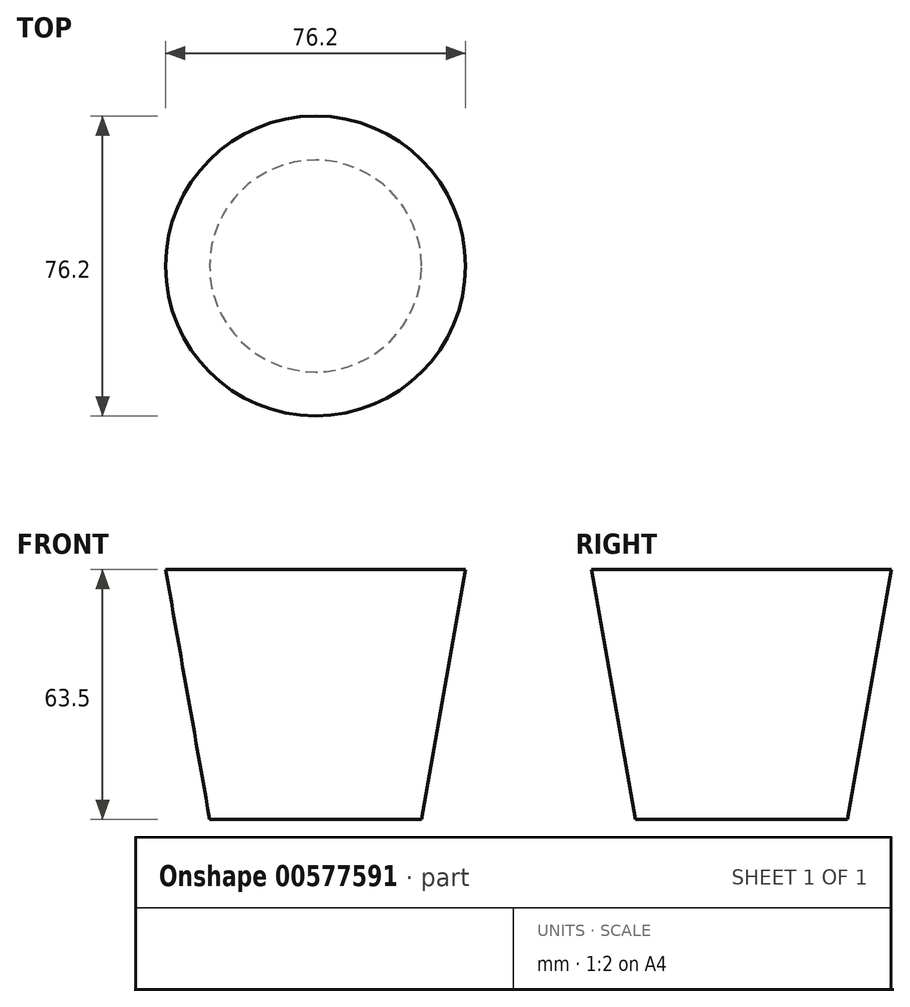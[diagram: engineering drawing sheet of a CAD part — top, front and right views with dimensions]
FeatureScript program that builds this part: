
annotation { "Feature Type Name" : "Feature", "Feature Type Description" : "" }
export const myFeature = defineFeature(function(context is Context, id is Id, definition is map)
    precondition{}
    {
        {
            var Q0;
            Q0=qCreatedBy(makeId("Front.planeOp"),FACE);
            var sketch = newSketch(context, id + "F0", { "sketchPlane" : qUnion([Q0])});
            skLineSegment(sketch, "E0", {"start": v(0, 63.5) * mm, "end": v(-38.1, 63.5) * mm});
            skLineSegment(sketch, "E1", {"start": v(-38.1, 63.5) * mm, "end": v(-26.9, 0) * mm});
            skLineSegment(sketch, "E2", {"start": v(-26.9, 0) * mm, "end": v(0, 0) * mm});
            skLineSegment(sketch, "E3", {"start": v(0, 0) * mm, "end": v(0, 63.5) * mm});
            skSolve(sketch);
        }
        {
            var Q0;
            Q0=makeQuery(id+"F0.imprint","IMPRINT",FACE,{"disambiguationData":[TD([[makeQuery(id+"F0.imprint","IMPRINT",EDGE,{"derivedFrom":sQuery(id+"F0.wireOp",EDGE,"E0")}),1.0]])]});
            var Q1;
            Q1=sQuery(id+"F0.wireOp",EDGE,"E3");
            revolve(context, id + "F1", {"entities" : qUnion([Q0]), "axis" : qUnion([Q1]), "revolveType" : RevolveType.FULL});
        }
    });
